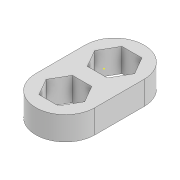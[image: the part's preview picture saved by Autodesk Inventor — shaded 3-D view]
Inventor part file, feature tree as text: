
AUTODESK INVENTOR PART (.ipt)
format: ipt  version: 2022 (Build 260153000, 153)  size: 230,400 bytes
history: native  units: mm
features: sketch x2, extrude x1
ambient origin geometry x8: Origin, YZ Plane, XZ Plane, XY Plane, X Axis, Y Axis, Z Axis, Center Point
bodies: Solid1 (feature_tree)
feature tree (3):
  extrude  "Extrusion1"  Depth=8.8mm
  sketch  "Sketch2"  dims[d2=25.0mm d3=35.0mm d4=35.0mm d5=15.0mm d6=12.0mm d7=0.0mm]
  sketch  "Sketch1"  dims[d0=8.5mm d1=8.8mm]
